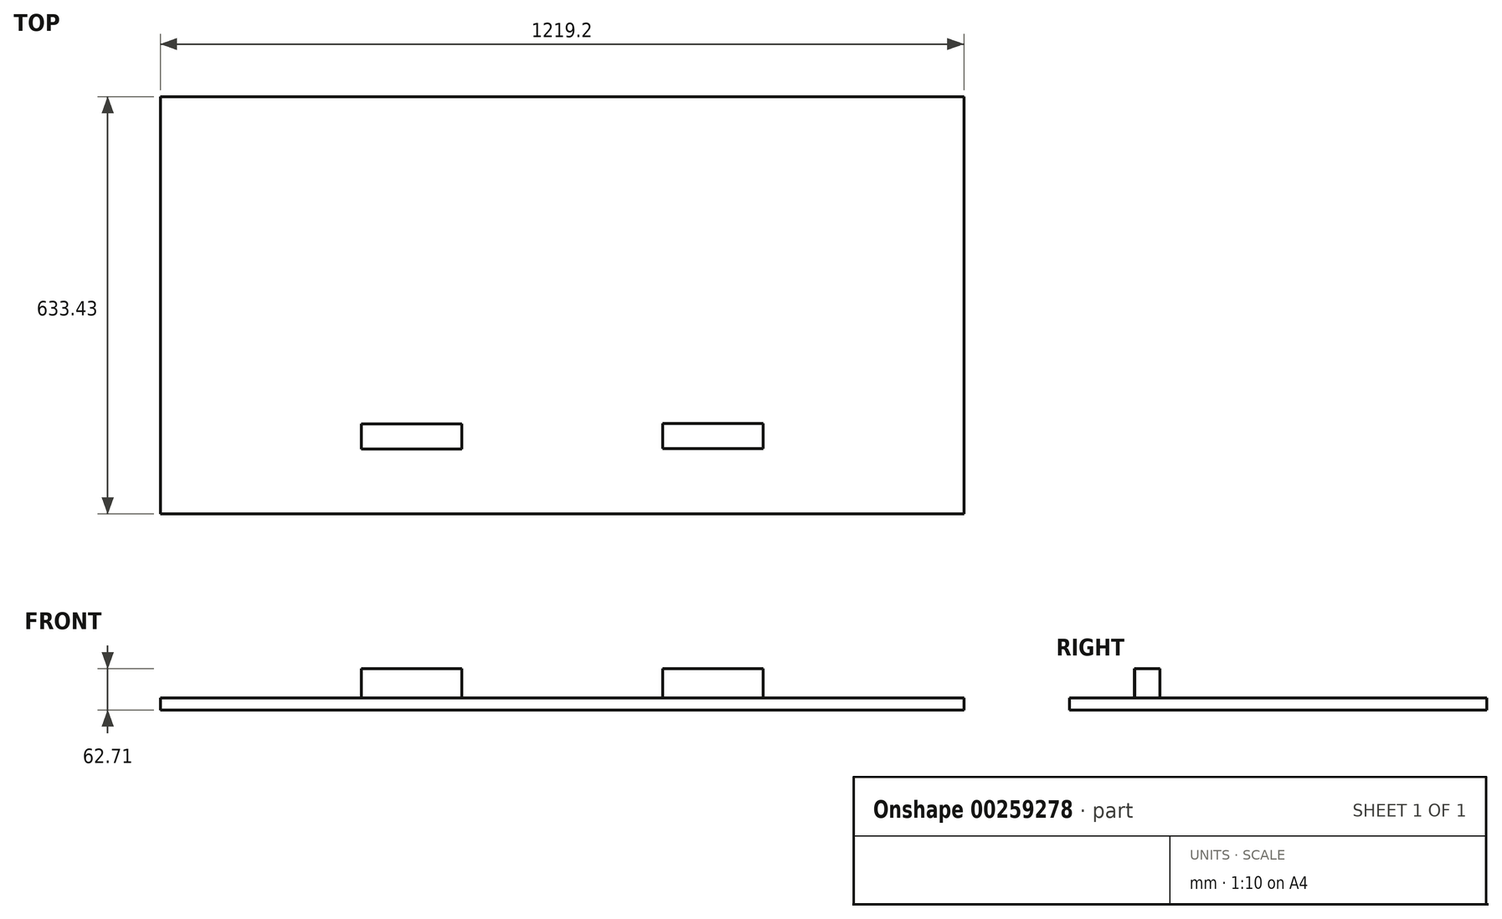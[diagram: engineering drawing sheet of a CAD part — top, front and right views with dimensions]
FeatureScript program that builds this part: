
annotation { "Feature Type Name" : "Feature", "Feature Type Description" : "" }
export const myFeature = defineFeature(function(context is Context, id is Id, definition is map)
    precondition{}
    {
        {
            var Q0;
            Q0=qCreatedBy(makeId("Top.planeOp"),FACE);
            var sketch = newSketch(context, id + "F0", { "sketchPlane" : qUnion([Q0])});
            skLineSegment(sketch, "E0.bottom", {"start": v(0, 0) * mm, "end": v(-1219.2, 0) * mm});
            skLineSegment(sketch, "E0.top", {"start": v(0, 633.43) * mm, "end": v(-1219.2, 633.43) * mm});
            skLineSegment(sketch, "E0.left", {"start": v(0, 0) * mm, "end": v(0, 633.43) * mm});
            skLineSegment(sketch, "E0.right", {"start": v(-1219.2, 0) * mm, "end": v(-1219.2, 633.43) * mm});
            skSolve(sketch);
        }
        {
            var Q0;
            Q0=qSketchRegion(id+"F0",true);
            extrude(context, id + "F1", {"entities" : qUnion([Q0]), "depth" : 18.26 * mm});
        }
        {
            var Q0;
            Q0=makeQuery(id+"F1.opExtrude","CAP_FACE",FACE,{"disambiguationData":[OSD([sQuery(id+"F0.wireOp",EDGE,"E0.bottom"),sQuery(id+"F0.wireOp",EDGE,"E0.top"),sQuery(id+"F0.wireOp",EDGE,"E0.left"),sQuery(id+"F0.wireOp",EDGE,"E0.right")])],"isStart":false});
            var sketch = newSketch(context, id + "F2", { "sketchPlane" : qUnion([Q0])});
            skLineSegment(sketch, "E1.bottom", {"start": v(-914.4, 136.66) * mm, "end": v(-762, 136.66) * mm});
            skLineSegment(sketch, "E1.top", {"start": v(-914.4, 98.56) * mm, "end": v(-762, 98.56) * mm});
            skLineSegment(sketch, "E1.left", {"start": v(-914.4, 136.66) * mm, "end": v(-914.4, 98.56) * mm});
            skLineSegment(sketch, "E1.right", {"start": v(-762, 136.66) * mm, "end": v(-762, 98.56) * mm});
            skLineSegment(sketch, "E2.bottom", {"start": v(-457.2, 137.4) * mm, "end": v(-304.8, 137.4) * mm});
            skLineSegment(sketch, "E2.top", {"start": v(-457.2, 99.3) * mm, "end": v(-304.8, 99.3) * mm});
            skLineSegment(sketch, "E2.left", {"start": v(-457.2, 137.4) * mm, "end": v(-457.2, 99.3) * mm});
            skLineSegment(sketch, "E2.right", {"start": v(-304.8, 137.4) * mm, "end": v(-304.8, 99.3) * mm});
            skLineSegment(sketch, "E3", {"start": v(-914.4, 117.6) * mm, "end": v(-1219.2, 117.6) * mm, "construction": true});
            skLineSegment(sketch, "E4", {"start": v(-762, 117.6) * mm, "end": v(-457.2, 117.6) * mm, "construction": true});
            skLineSegment(sketch, "E5", {"start": v(-304.8, 118.35) * mm, "end": v(0, 118.35) * mm, "construction": true});
            skSolve(sketch);
        }
        {
            var Q0;
            Q0=makeQuery(id+"F2.imprint","IMPRINT",FACE,{"disambiguationData":[TD([[makeQuery(id+"F2.imprint","IMPRINT",EDGE,{"derivedFrom":sQuery(id+"F2.wireOp",EDGE,"E1.bottom")}),-1.0]])]});
            var Q1;
            Q1=makeQuery(id+"F2.imprint","IMPRINT",FACE,{"disambiguationData":[TD([[makeQuery(id+"F2.imprint","IMPRINT",EDGE,{"derivedFrom":sQuery(id+"F2.wireOp",EDGE,"E2.bottom")}),-1.0]])]});
            extrude(context, id + "F3", {"entities" : qUnion([Q0, Q1]), "operationType" : NewBodyOperationType.ADD, "depth" : 44.45 * mm});
        }
    });
